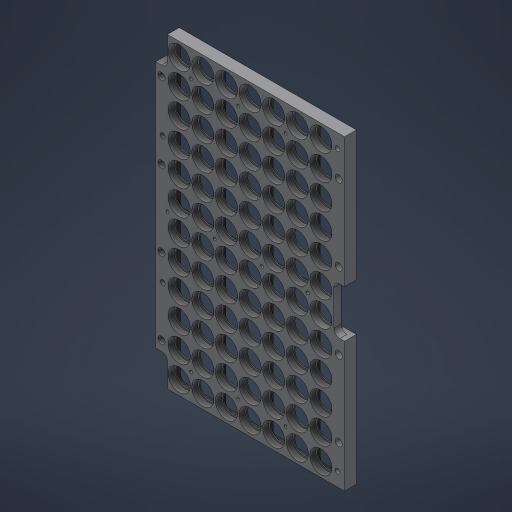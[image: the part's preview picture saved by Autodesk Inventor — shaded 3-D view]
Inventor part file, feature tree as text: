
AUTODESK INVENTOR PART (.ipt)
format: ipt  version: 2024.3 (Build 283343010, 343A)  size: 1,401,344 bytes
history: native  units: mm
features: sketch x7, extrude x6, hole x5, fillet x2, pattern_linear x1, projected_geometry x1
ambient origin geometry x8: Origin, YZ Plane, XZ Plane, XY Plane, X Axis, Y Axis, Z Axis, Center Point
bodies: Volumenkörper1 (feature_tree)
feature tree (22):
  sketch  "Skizze1"  dims[d0=160.0mm d1=260.0mm]
  extrude  "Extrusion1"  Depth=260.0mm
  hole  "Bohrung1"  [1 undecoded]
  pattern_linear  "Rechteckige Anordnung1"  Count1=6 Spacing1=43.0mm
  sketch  "Skizze2"  dims[d2=10.0mm d3=0.0mm d4=18.0mm d5=60.0mm d7=43.0mm d8=70.0mm d10=20.0mm]
  extrude  "Extrusion2"  Depth=70.0mm
  sketch  "Skizze3"  dims[d16=21.5mm d19=70.0mm d21=20.0mm]
  sketch  "Skizze4"  dims[d22=60.0mm d24=43.0mm d69=15.0mm]
  extrude  "Extrusion6"  Depth=60.0mm
  extrude  "Extrusion7"  Depth=70.0mm
  hole  "Bohrung5"  [1 undecoded]
  hole  "Bohrung6"  [1 undecoded]
  extrude  "Extrusion9"  Depth=10.0mm TaperAngle=0.0deg
  hole  "Bohrung7"  [1 undecoded]
  fillet  "Rundung4"  Radius=157.7mm
  sketch  "Skizze9"  dims[d84=5.0mm d85=60.0mm d89=10.0mm d90=0.0mm d101=25.0mm d113=157.7mm d119=8.0mm d121=6.0mm d124=33.25mm d125=64.5mm d126=6.0mm d127=10.75mm d129=7.0mm d130=7.0mm d132=3.0mm d134=10.75mm d135=9.5mm d136=3.0mm d142=6.0mm d143=5.0mm d144=5.0mm d145=4.0mm d146=6.0mm d147=4.0mm d148=2.0mm d149=90.0deg d150=8.0mm d151=20.594885mm d160=8.0mm d162=3.0mm d165=20.0mm d166=5.75mm d169=7.0mm d170=7.0mm d171=3.64mm d172=10.75mm d180=1.8mm d181=1.8mm d182=5.0mm d184=8.95mm d185=8.95mm d186=4.0mm d187=0.0mm d190=40.0mm d191=20.0mm d192=0.0mm d193=0.0mm d195=60.0mm d196=60.0mm d197=4.0mm d198=6.0mm d199=6.0mm d200=5.0mm d201=90.0deg d202=8.0mm d203=20.594885mm d204=4.0mm d205=6.0mm d206=6.0mm d207=5.0mm d208=90.0deg d209=8.0mm d210=20.594885mm d222=37.9mm d223=127.4mm d224=5.0mm d225=30.0mm d227=40.0mm d228=20.0mm d230=129.0mm d233=0.0mm d234=0.0mm d236=5.0mm d237=5.0mm d238=2.4mm d239=0.0mm d240=9.0mm d241=2.5mm d242=6.0mm d243=19.05mm d244=4.775mm d245=90.0deg d246=8.0mm d247=20.594885mm d251=40.0mm d252=107.5mm d254=3.0mm d256=3.0mm d257=6.0mm d258=3.0mm d259=5.0mm d260=40.0mm d261=40.0mm d262=20.0mm d263=0.0mm d264=0.0mm d265=200.0mm d266=300.0mm d267=5.0mm d268=5.0mm d275=5.0mm d276=5.0mm d277=5.0mm d278=8.95mm d280=107.5mm d281=107.5mm d118=0.5mm d120=0.5mm]
  extrude  "Extrusion10"  Depth=8.0mm
  fillet  "Rundung3"  Radius=6.0mm
  hole  "Bohrung3"  [1 undecoded]
  sketch  "Skizze5"  dims[d70=16.0mm d71=6.0mm d72=18.7mm d73=5.0mm d74=90.0deg d75=8.0mm d76=20.594885mm d77=70.0mm d79=20.0mm]
  sketch  "Skizze8"  dims[d80=0.0mm d83=10.0mm]
  projected_geometry  "Projizierte Kontur3"
note: 5 required parameter values undecoded (feature->parameter linkage not recoverable at this tier; creation-order binding heuristic only, values carry confidence <= 0.55)
